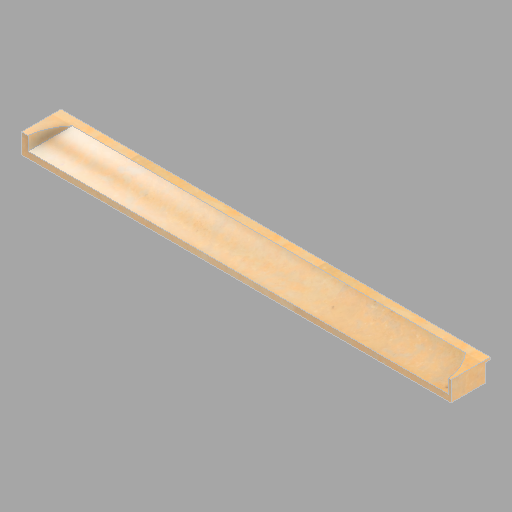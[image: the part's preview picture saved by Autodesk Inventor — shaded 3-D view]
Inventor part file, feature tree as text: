
AUTODESK INVENTOR PART (.ipt)
format: ipt  version: 2022.2 (Build 262287010, 287A)  size: 192,000 bytes
history: native  units: in
note: dims shown in document units (in); Inventor stores cm internally (conversion verified against a paired STEP export)
features: revolve x2, direct_edit x1
ambient origin geometry x8: Origin, YZ Plane, XZ Plane, XY Plane, X Axis, Y Axis, Z Axis, Center Point
bodies: Solid1 (feature_tree), Body1 (feature_tree)
feature tree (3):
  direct_edit  "Direct Edit1"
  revolve  "Rotate1"  Angle=180.0deg
  revolve  "Rotate2"  [1 undecoded]
note: 1 required parameter value undecoded (feature->parameter linkage not recoverable at this tier; creation-order binding heuristic only, values carry confidence <= 0.55)
